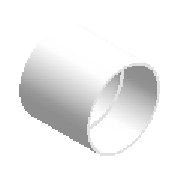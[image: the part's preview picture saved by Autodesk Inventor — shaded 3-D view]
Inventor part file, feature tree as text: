
AUTODESK INVENTOR PART (.ipt)
format: ipt  version: 2023.1 (Build 271208000, 208)  size: 165,376 bytes
history: native  units: mm (DEFAULTED — no unit token found)
features: other x6, sketch x1
ambient origin geometry x8: Origin, YZ Plane, XZ Plane, XY Plane, X Axis, Y Axis, Z Axis, Center Point
bodies: Solid1 (feature_tree)
feature tree (7):
  other  "Work Point1"
  other  "Work Point2"
  other  "Work Axis1"
  other  "Work Point3"
  other  "Work Axis2"
  other  "Work Point4"
  sketch  "Sketch1"  dims[d1=89.45mm d2=88.65mm d0=89.45mm d3=88.65mm d4=40.0mm d5=96.25mm d107=90.0deg d6=77.2mm d7=84.0mm]
